# Revit family: BLAUBERG-KOMFORT_EC_SB350
name_source: partatom
category: Mechanical Equipment
units: mm (PartAtom-declared; Revit-internal decimal feet)

## family parameters
Always vertical = Yes
Classification = None
Cut with Voids When Loaded = No
OmniClass Number = 23.75.35.14
OmniClass Title = Air Handling Units
Part Type = Normal
Room Calculation Point = No
Round Connector Dimension = Use Diameter
Shared = No
Work Plane-Based = No

## types (4) — shared parameters
B = 600 mm
B1 = 583 mm
B3 = 14 mm  [stored 0.0459318 ft]
BackFeetD = 20 mm  [stored 0.0656168 ft]
Casing Material = Painted Steel White
Current = 1 A
D = 160 mm  [stored 0.524934 ft]
Description = Air Handling Unit
Duct Connection Diameter = 160 mm  [stored 0.524934 ft]
ElBoxA = 160 mm  [stored 0.524934 ft]
ElBoxB = 345 mm  [stored 1.13189 ft]
ElConA = 342 mm  [stored 1.12205 ft]
Extract Air Filter = G4
Family Version = 1.0
Front Maintenance Zone Height = 600 mm
Front Maintenance Zone Length = 730 mm  [stored 2.39501 ft]
Front Maintenance Zone Width = 675 mm  [stored 2.21457 ft]
H1 = 675 mm  [stored 2.21457 ft]
H3 = 60 mm  [stored 0.19685 ft]
HDuctCon = 50 mm  [stored 0.164042 ft]
Heat Exchanger Type = counter-flow
L = 730 mm  [stored 2.39501 ft]
L1 = 426 mm  [stored 1.39764 ft]
L2 = 230 mm  [stored 0.754593 ft]
Load Classification = HVAC
Maintenance Zone Material = Maintenance Zone
Manufacturer = Blauberg
Maximum Air Flow = 450 m³/h
Metal Material = Metal Zinc
Number of Poles = 1
Plastic Material = Polypropylene Black
Power = 178 W
Power Factor = 1
RPM (min-1) = 3200
Sound Pressure Level at 3 m (dBA) = 28
Supply Air Filter = F7 (optionally G4)
Transported Air Temperature (°C) = –25 …+40
URL = https://blaubergventilatoren.de
Voltage = 230 V
Weight = 64.00 kg
dBFeets = 52 mm
dLFeets = 52 mm

## per-type parameters (varying)
| type | Ddrain | Drain Connection Diameter | DrainConB | DrainPipe | Heat Exchanger Material | Heat recovery efficiency (%) | Model | SEC Class | Type Comments |
| KOMFORT EC SB350 S21 | 18 mm  [stored 0.0590551 ft] | 18 mm  [stored 0.0590551 ft] | 292 mm  [stored 0.958005 ft] | Yes | polystyrene | 85..92 | KOMFORT EC SB160-E S14 | A+ | Air Handling Unit KOMFORT EC SB160-E S14 |
| KOMFORT EC SB350 S14 | 18 mm  [stored 0.0590551 ft] | 18 mm  [stored 0.0590551 ft] | 293 mm | Yes | polystyrene | 85..92 | KOMFORT EC SB350 S21 | A+ | Air Handling Unit KOMFORT EC SB350 S21 |
| KOMFORT EC SB350-E S21 | 1 mm  [stored 0.00328084 ft] | 0 mm  [stored 0 ft] | 294 mm  [stored 0.964567 ft] | No | enthalpy | 73..91 | KOMFORT EC SB350-E S21 | A | Air Handling Unit KOMFORT EC SB350-E S21 |
| KOMFORT EC SB350-E S14 | 1 mm  [stored 0.00328084 ft] | 0 mm  [stored 0 ft] | 295 mm  [stored 0.967848 ft] | No | enthalpy | 73..91 | KOMFORT EC SB350 S14 | A | Air Handling Unit KOMFORT EC SB350 S14 |

note: [stored X ft] marks values corroborated as IEEE doubles in the binary element streams (Revit-internal decimal feet)

## geometry (parser evidence)
native form markers: Sweep x5
no freeform markers — native parametric forms only
